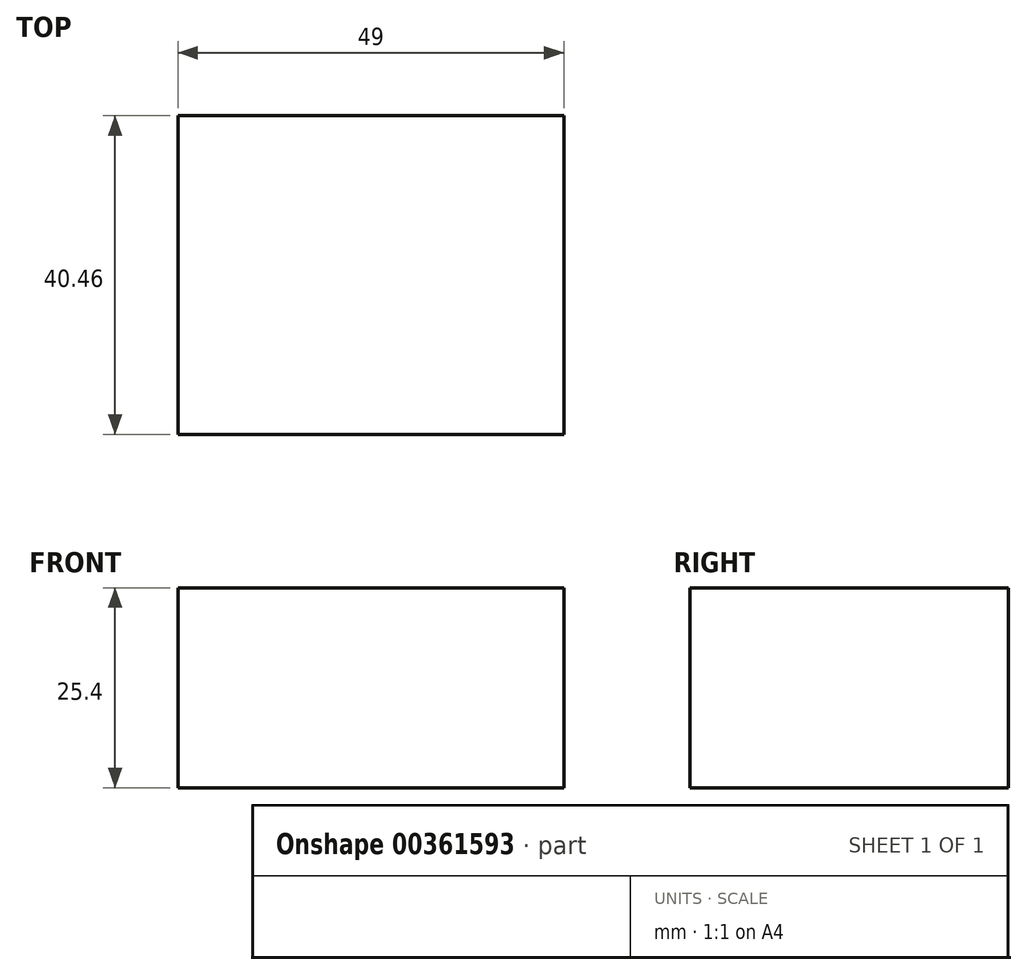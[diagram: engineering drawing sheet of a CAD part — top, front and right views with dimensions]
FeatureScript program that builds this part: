
annotation { "Feature Type Name" : "Feature", "Feature Type Description" : "" }
export const myFeature = defineFeature(function(context is Context, id is Id, definition is map)
    precondition{}
    {
        {
            var Q0;
            Q0=qCreatedBy(makeId("Top.planeOp"),FACE);
            var sketch = newSketch(context, id + "F0", { "sketchPlane" : qUnion([Q0])});
            skLineSegment(sketch, "E0.bottom", {"start": v(-24.15, 22.2) * mm, "end": v(24.85, 22.2) * mm});
            skLineSegment(sketch, "E0.top", {"start": v(-24.15, -18.25) * mm, "end": v(24.85, -18.25) * mm});
            skLineSegment(sketch, "E0.left", {"start": v(-24.15, 22.2) * mm, "end": v(-24.15, -18.25) * mm});
            skLineSegment(sketch, "E0.right", {"start": v(24.85, 22.2) * mm, "end": v(24.85, -18.25) * mm});
            skSolve(sketch);
        }
        {
            var Q0;
            Q0 = qSketchRegion(id + "F0", true);
            extrude(context, id + "F1", {"entities" : qUnion([Q0]), "depth" : 25.4 * mm});
        }
    });
